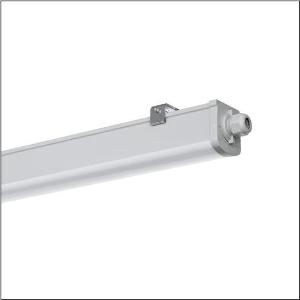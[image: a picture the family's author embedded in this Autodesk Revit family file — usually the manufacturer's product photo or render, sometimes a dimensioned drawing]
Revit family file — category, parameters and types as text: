
# Revit family: monsun_r__31_51fa207p430b_b845
name_source: partatom
category: Lighting Fixtures
units: mm (PartAtom-declared; Revit-internal decimal feet)

## family parameters
Cut with Voids When Loaded = No
Host = Face
Light Source = No
Part Type = Normal
Room Calculation Point = No
Round Connector Dimension = Use Diameter
Shared = No

## types (1)
- Monsun® 31 (1 x LED, 3800 lm, 28 W, 4000K)
    Apparent Load = 28 VA
    CIE Flux Codes = 42 72 91 92 100
    Color Rendering = 80
    Color Temperature = 4000K
    Default Elevation = 1800 mm
    Description = Monsun® 31, damp-proof luminaire, primary optical cover: diffuser, of PC, frosted, light emission: direct distribution, primary light characteristic: symmetric, installation type: surface-mounted, LED, rated luminous flux: 3.800lm, luminous efficacy: 136lm/W, light colour: 840, colour temperature: 4000K, control gear: ECG, with terminal, 3+1-pole, max. 2.5mm², through-wiring: 3x 2.5mm² + 1x 1.5mm², mains connection: 220..240V, AC, 50/60Hz, rated input power: 28W, housing, luminaire housing, of PC, light grey (RAL 7035), length: 1.458mm, width: 68mm, height: 76mm, protection rating (complete): IP66, insulation class (complete): insulation class II (safety insulation), certification: CE, ENEC, UKCA, protection symbol: D, impact resistance: IK08, permissible operating ambient temperature: -20..+40°C, corresponds to IFS (International Featured Standards) requirements for safety and quality in the food industry, contact your sales advisor before using the luminaires in applications with unclear chemical exposure, large temperature fluctuations or condensation-forming humidity, packaging unit: 1 piece
    Height = 77 mm
    Lamp = 1 x LED
    Lamp Light Flux = 3800 lm
    Lamp Power = 28 W
    Lamp count = 1
    Length = 1518 mm
    Luminous efficacy = 136 lm/W
    Manufacturer = Siteco
    ModVariant = No
    Model = 51FA207P430B
    Mounting Place = Ceiling
    Mounting Type = Surface mounted
    Number of Poles = 1
    OnlyDefault = Yes
    Power Factor = 1
    Product Name = Monsun® 31
    Product group = damp-proof luminaire
    ProductGroupID = 301
    Protection Class = Protection class II
    Protection Degree = IP 66
    RLX_Detail_Level = 1
    RLX_Emergency_Light_Flux = 0 lm
    RLX_Emergency_Type = 0
    RLX_Emergency_Type_DB = No
    RlxData = <blob elided: 33117 chars, md5=451eaad9>
    Socket = socket
    Standby Power = 0 W
    System Light Flux = 3800 lm
    System Power = 28 W
    Type Comments = Product without accessories
    Type Image = l_1006174.jpg
    URL = http://relux.com
    VarID = ---
    Voltage = 0 V
    Weight = 0.00 kg
    Width = 69 mm

## geometry (parser evidence)
native form markers: Blend x4, Sweep x12
no freeform markers — native parametric forms only
